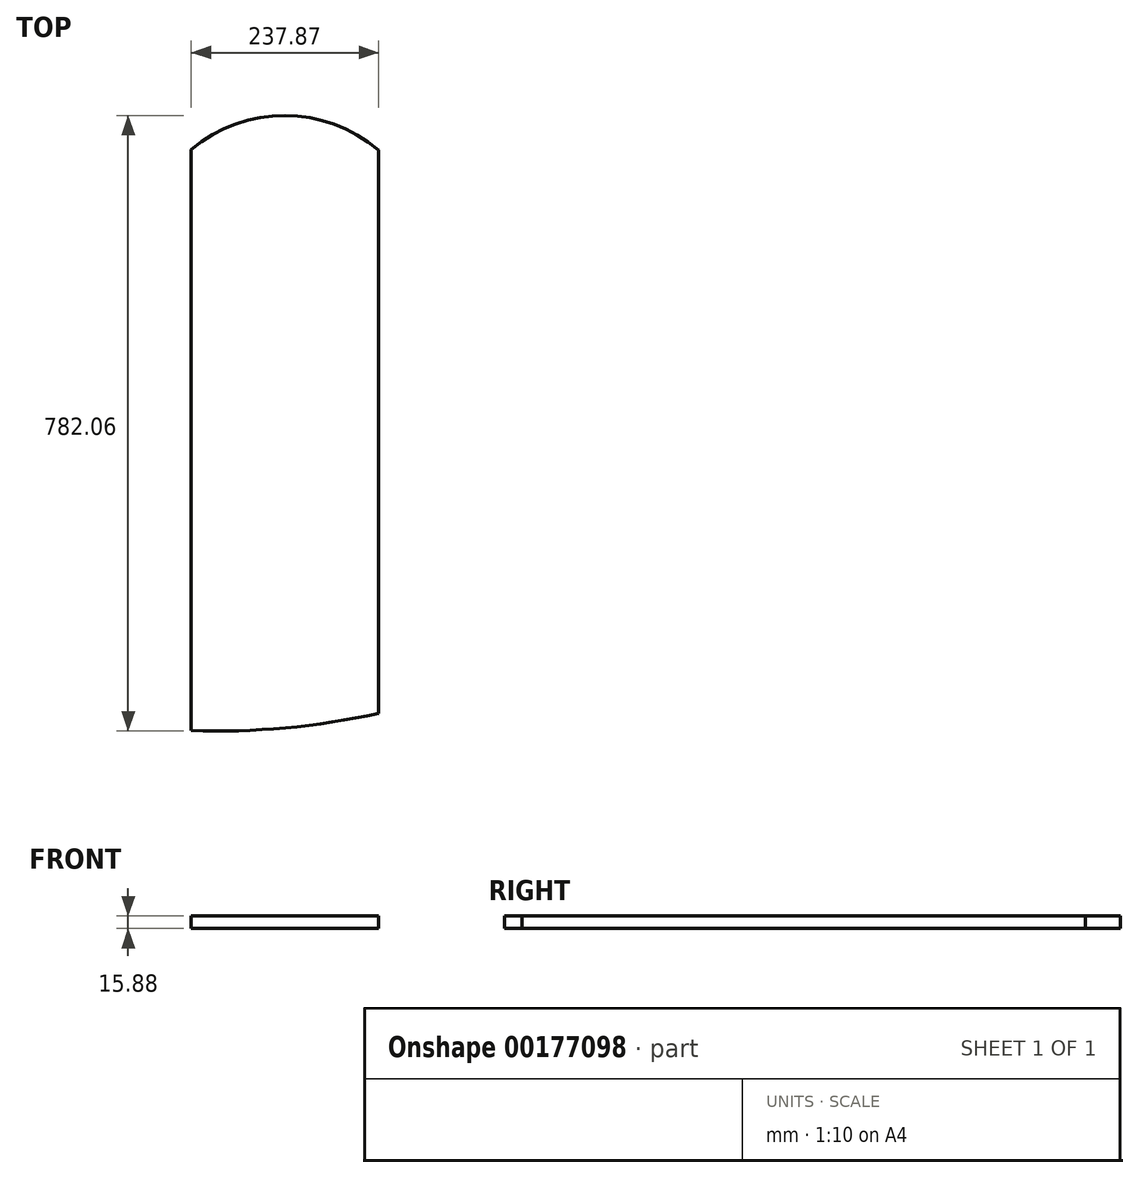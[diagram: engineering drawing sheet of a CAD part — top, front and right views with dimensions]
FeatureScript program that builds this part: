
annotation { "Feature Type Name" : "Feature", "Feature Type Description" : "" }
export const myFeature = defineFeature(function(context is Context, id is Id, definition is map)
    precondition{}
    {
        {
            var Q0;
            Q0=qCreatedBy(makeId("Top.planeOp"),FACE);
            var sketch = newSketch(context, id + "F0", { "sketchPlane" : qUnion([Q0])});
            skLineSegment(sketch, "E0", {"start": v(0, 0) * mm, "end": v(0, 781.05) * mm, "construction": true});
            skLineSegment(sketch, "E1", {"start": v(0, 781.05) * mm, "end": v(267.61, 781.05) * mm, "construction": true});
            skLineSegment(sketch, "E2", {"start": v(0, 0) * mm, "end": v(-47.1, 0) * mm, "construction": true});
            skLineSegment(sketch, "E3", {"start": v(128.4, 737.12) * mm, "end": v(128.4, 21.94) * mm});
            skArc(sketch, "E4", {"start": v(128.4, 737.12) * mm, "mid": v(9.6, 781.47) * mm, "end": v(-109.47, 737.9) * mm});
            skArc(sketch, "E5", {"start": v(-109.47, 0) * mm, "mid": v(10.16, 3.38) * mm, "end": v(128.4, 21.94) * mm});
            skLineSegment(sketch, "E6", {"start": v(-109.47, 737.9) * mm, "end": v(-109.47, 0) * mm});
            skSolve(sketch);
        }
        {
            var Q0;
            Q0 = qSketchRegion(id + "F0", true);
            extrude(context, id + "F1", {"entities" : qUnion([Q0]), "depth" : 15.88 * mm});
        }
    });
